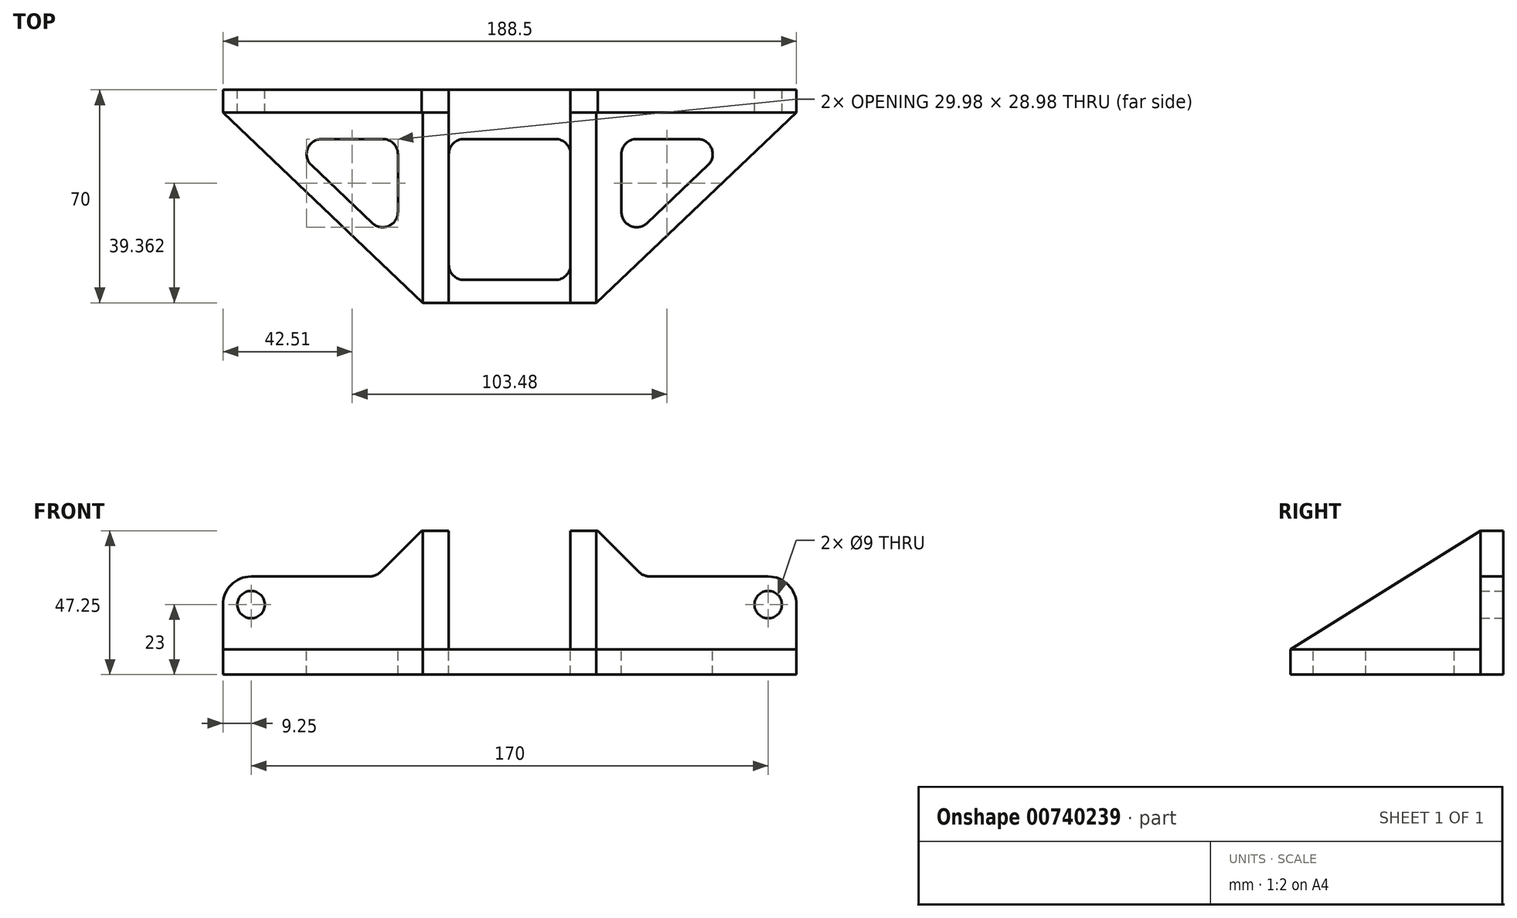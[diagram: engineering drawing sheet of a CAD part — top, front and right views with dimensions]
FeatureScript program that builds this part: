
annotation { "Feature Type Name" : "Feature", "Feature Type Description" : "" }
export const myFeature = defineFeature(function(context is Context, id is Id, definition is map)
    precondition{}
    {
        {
            var Q0;
            Q0=qCreatedBy(makeId("Front.planeOp"),FACE);
            var sketch = newSketch(context, id + "F0", { "sketchPlane" : qUnion([Q0])});
            skLineSegment(sketch, "E0", {"start": v(0, 0) * mm, "end": v(94.25, 0) * mm});
            skLineSegment(sketch, "E1", {"start": v(94.25, 0) * mm, "end": v(94.25, 23) * mm});
            skLineSegment(sketch, "E2", {"start": v(85, 32.25) * mm, "end": v(44, 32.25) * mm});
            skLineSegment(sketch, "E3", {"start": v(44, 32.25) * mm, "end": v(29, 47.25) * mm});
            skLineSegment(sketch, "E4", {"start": v(29, 47.25) * mm, "end": v(20, 47.25) * mm});
            skLineSegment(sketch, "E5", {"start": v(20, 47.25) * mm, "end": v(20, 8.25) * mm});
            skLineSegment(sketch, "E6", {"start": v(20, 8.25) * mm, "end": v(0, 8.25) * mm});
            skLineSegment(sketch, "E7", {"start": v(0, -10.9) * mm, "end": v(0, 33.84) * mm, "construction": true});
            skCircle(sketch, "E8", {"center": v(85, 23) * mm, "radius": 4.5 * mm});
            skPoint(sketch, "E9.visualSharp", {"position": v(94.25, 32.25) * mm});
            skArc(sketch, "E9.filletArc", {"start": v(94.25, 23) * mm, "mid": v(91.54, 29.54) * mm, "end": v(85, 32.25) * mm});
            skLineSegment(sketch, "E10.MirrorCS", {"start": v(-29, 47.25) * mm, "end": v(-20, 47.25) * mm});
            skPoint(sketch, "E11.MirrorP", {"position": v(-94.25, 32.25) * mm});
            skLineSegment(sketch, "E12.MirrorCS", {"start": v(0, 0) * mm, "end": v(-94.25, 0) * mm});
            skLineSegment(sketch, "E13.MirrorCS", {"start": v(-94.25, 0) * mm, "end": v(-94.25, 23) * mm});
            skLineSegment(sketch, "E14.MirrorCS", {"start": v(-44, 32.25) * mm, "end": v(-29, 47.25) * mm});
            skLineSegment(sketch, "E15.MirrorCS", {"start": v(-85, 32.25) * mm, "end": v(-44, 32.25) * mm});
            skLineSegment(sketch, "E16.MirrorCS", {"start": v(-20, 47.25) * mm, "end": v(-20, 8.25) * mm});
            skLineSegment(sketch, "E17.MirrorCS", {"start": v(-20, 8.25) * mm, "end": v(0, 8.25) * mm});
            skArc(sketch, "E18.MirrorCS", {"start": v(-94.25, 23) * mm, "mid": v(-91.54, 29.54) * mm, "end": v(-85, 32.25) * mm});
            skCircle(sketch, "E19.MirrorC", {"center": v(-85, 23) * mm, "radius": 4.5 * mm});
            skSolve(sketch);
        }
        {
            var Q0;
            Q0 = qSketchRegion(id + "F0", true);
            extrude(context, id + "F1", {"entities" : qUnion([Q0]), "depth" : 7.5 * mm, "offsetDistance" : 25.4 * mm});
        }
        {
            var Q0;
            Q0=makeQuery(id+"F1.opExtrude","CAP_FACE",FACE,{"disambiguationData":[OSD([sQuery(id+"F0.wireOp",EDGE,"E0"),sQuery(id+"F0.wireOp",EDGE,"E1"),sQuery(id+"F0.wireOp",EDGE,"E2"),sQuery(id+"F0.wireOp",EDGE,"E3"),sQuery(id+"F0.wireOp",EDGE,"E4"),sQuery(id+"F0.wireOp",EDGE,"E5"),sQuery(id+"F0.wireOp",EDGE,"E6"),sQuery(id+"F0.wireOp",EDGE,"E8"),sQuery(id+"F0.wireOp",EDGE,"E9.filletArc"),sQuery(id+"F0.wireOp",EDGE,"E10.MirrorCS"),sQuery(id+"F0.wireOp",EDGE,"E12.MirrorCS"),sQuery(id+"F0.wireOp",EDGE,"E13.MirrorCS"),sQuery(id+"F0.wireOp",EDGE,"E14.MirrorCS"),sQuery(id+"F0.wireOp",EDGE,"E15.MirrorCS"),sQuery(id+"F0.wireOp",EDGE,"E16.MirrorCS"),sQuery(id+"F0.wireOp",EDGE,"E17.MirrorCS"),sQuery(id+"F0.wireOp",EDGE,"E18.MirrorCS"),sQuery(id+"F0.wireOp",EDGE,"E19.MirrorC")])],"isStart":false});
            var sketch = newSketch(context, id + "F2", { "sketchPlane" : qUnion([Q0])});
            skLineSegment(sketch, "E20.bottom", {"start": v(-94.25, 0) * mm, "end": v(94.25, 0) * mm});
            skLineSegment(sketch, "E20.top", {"start": v(-94.25, 8.25) * mm, "end": v(94.25, 8.25) * mm});
            skLineSegment(sketch, "E20.left", {"start": v(-94.25, 0) * mm, "end": v(-94.25, 8.25) * mm});
            skLineSegment(sketch, "E20.right", {"start": v(94.25, 0) * mm, "end": v(94.25, 8.25) * mm});
            skSolve(sketch);
        }
        {
            var Q0;
            Q0 = qSketchRegion(id + "F2", true);
            extrude(context, id + "F3", {"entities" : qUnion([Q0]), "operationType" : NewBodyOperationType.ADD, "depth" : 62.5 * mm, "offsetDistance" : 25.4 * mm});
        }
        {
            var Q0;
            Q0=makeQuery(id+"F3.boolean.opBoolean","MERGE",FACE,{"derivedFrom":[makeQuery(id+"F1.opExtrude","SWEPT_FACE",FACE,{"disambiguationData":[OSD([sQuery(id+"F0.wireOp",EDGE,"E6"),sQuery(id+"F0.wireOp",EDGE,"E17.MirrorCS")])]}),makeQuery(id+"F3.opExtrude","SWEPT_FACE",FACE,{"disambiguationData":[OSD([sQuery(id+"F2.wireOp",EDGE,"E20.top")])]})]});
            var sketch = newSketch(context, id + "F4", { "sketchPlane" : qUnion([Q0])});
            skLineSegment(sketch, "E21", {"start": v(-61.75, -16.15) * mm, "end": v(-41.75, -16.15) * mm});
            skLineSegment(sketch, "E22", {"start": v(-36.75, -21.15) * mm, "end": v(-36.75, -40.16) * mm});
            skLineSegment(sketch, "E23", {"start": v(-45.2, -43.78) * mm, "end": v(-65.2, -24.77) * mm});
            skLineSegment(sketch, "E24", {"start": v(0, -16.15) * mm, "end": v(-15, -16.15) * mm});
            skLineSegment(sketch, "E25", {"start": v(-20, -21.15) * mm, "end": v(-20, -57.5) * mm});
            skLineSegment(sketch, "E26", {"start": v(-15, -62.5) * mm, "end": v(0, -62.5) * mm});
            skLineSegment(sketch, "E27", {"start": v(-94.25, -7.5) * mm, "end": v(-28.5, -70) * mm});
            skLineSegment(sketch, "E28", {"start": v(-28.5, -70) * mm, "end": v(-94.25, -70) * mm});
            skLineSegment(sketch, "E29", {"start": v(-94.25, -70) * mm, "end": v(-94.25, -7.5) * mm});
            skLineSegment(sketch, "E30", {"start": v(0, 0) * mm, "end": v(0, -70) * mm, "construction": true});
            skPoint(sketch, "E31.visualSharp", {"position": v(-36.75, -16.15) * mm});
            skArc(sketch, "E31.filletArc", {"start": v(-36.75, -21.15) * mm, "mid": v(-38.21, -17.61) * mm, "end": v(-41.75, -16.15) * mm});
            skPoint(sketch, "E32.visualSharp", {"position": v(-74.26, -16.15) * mm});
            skArc(sketch, "E32.filletArc", {"start": v(-61.75, -16.15) * mm, "mid": v(-66.4, -19.3) * mm, "end": v(-65.2, -24.77) * mm});
            skPoint(sketch, "E33.visualSharp", {"position": v(-36.75, -51.81) * mm});
            skArc(sketch, "E33.filletArc", {"start": v(-45.2, -43.78) * mm, "mid": v(-39.78, -44.75) * mm, "end": v(-36.75, -40.16) * mm});
            skPoint(sketch, "E34.visualSharp", {"position": v(-20, -62.5) * mm});
            skArc(sketch, "E34.filletArc", {"start": v(-20, -57.5) * mm, "mid": v(-18.54, -61.04) * mm, "end": v(-15, -62.5) * mm});
            skPoint(sketch, "E35.visualSharp", {"position": v(-20, -16.15) * mm});
            skArc(sketch, "E35.filletArc", {"start": v(-15, -16.15) * mm, "mid": v(-18.54, -17.61) * mm, "end": v(-20, -21.15) * mm});
            skLineSegment(sketch, "E36.MirrorCS", {"start": v(0, -16.15) * mm, "end": v(15, -16.15) * mm});
            skLineSegment(sketch, "E37.MirrorCS", {"start": v(15, -62.5) * mm, "end": v(0, -62.5) * mm});
            skArc(sketch, "E38.MirrorCS", {"start": v(20, -57.5) * mm, "mid": v(18.54, -61.04) * mm, "end": v(15, -62.5) * mm});
            skArc(sketch, "E39.MirrorCS", {"start": v(15, -16.15) * mm, "mid": v(18.54, -17.61) * mm, "end": v(20, -21.15) * mm});
            skArc(sketch, "E40.MirrorCS", {"start": v(36.75, -21.15) * mm, "mid": v(38.21, -17.61) * mm, "end": v(41.75, -16.15) * mm});
            skPoint(sketch, "E41.MirrorP", {"position": v(36.75, -51.81) * mm});
            skPoint(sketch, "E42.MirrorP", {"position": v(20, -62.5) * mm});
            skPoint(sketch, "E43.MirrorP", {"position": v(74.26, -16.15) * mm});
            skPoint(sketch, "E44.MirrorP", {"position": v(20, -16.15) * mm});
            skLineSegment(sketch, "E45.MirrorCS", {"start": v(45.2, -43.78) * mm, "end": v(65.2, -24.77) * mm});
            skLineSegment(sketch, "E46.MirrorCS", {"start": v(36.75, -21.15) * mm, "end": v(36.75, -40.16) * mm});
            skLineSegment(sketch, "E47.MirrorCS", {"start": v(61.75, -16.15) * mm, "end": v(41.75, -16.15) * mm});
            skPoint(sketch, "E48.MirrorP", {"position": v(36.75, -16.15) * mm});
            skArc(sketch, "E49.MirrorCS", {"start": v(45.2, -43.78) * mm, "mid": v(39.78, -44.75) * mm, "end": v(36.75, -40.16) * mm});
            skLineSegment(sketch, "E50.MirrorCS", {"start": v(28.5, -70) * mm, "end": v(94.25, -70) * mm});
            skLineSegment(sketch, "E51.MirrorCS", {"start": v(20, -21.15) * mm, "end": v(20, -57.5) * mm});
            skLineSegment(sketch, "E52.MirrorCS", {"start": v(94.25, -7.5) * mm, "end": v(28.5, -70) * mm});
            skLineSegment(sketch, "E53.MirrorCS", {"start": v(94.25, -70) * mm, "end": v(94.25, -7.5) * mm});
            skArc(sketch, "E54.MirrorCS", {"start": v(61.75, -16.15) * mm, "mid": v(66.4, -19.3) * mm, "end": v(65.2, -24.77) * mm});
            skSolve(sketch);
        }
        {
            var Q0;
            Q0 = qSketchRegion(id + "F4", true);
            var Q1;
            Q1=makeQuery(id+"F3.boolean.opBoolean","MERGE",FACE,{"derivedFrom":[makeQuery(id+"F1.opExtrude","SWEPT_FACE",FACE,{"disambiguationData":[OSD([sQuery(id+"F0.wireOp",EDGE,"E0"),sQuery(id+"F0.wireOp",EDGE,"E12.MirrorCS")])]}),makeQuery(id+"F3.opExtrude","SWEPT_FACE",FACE,{"disambiguationData":[OSD([sQuery(id+"F2.wireOp",EDGE,"E20.bottom")])]})]});
            extrude(context, id + "F5", {"entities" : qUnion([Q0]), "operationType" : NewBodyOperationType.REMOVE, "endBound" : BoundingType.UP_TO_SURFACE, "oppositeDirection" : true, "depth" : 25.4 * mm, "endBoundEntityFace" : qUnion([Q1]), "offsetDistance" : 25.4 * mm});
        }
        {
            var Q0;
            Q0=makeQuery(id+"F1.opExtrude","SWEPT_FACE",FACE,{"disambiguationData":[OSD([sQuery(id+"F0.wireOp",EDGE,"E16.MirrorCS")])]});
            var sketch = newSketch(context, id + "F6", { "sketchPlane" : qUnion([Q0])});
            skLineSegment(sketch, "E55", {"start": v(-7.5, 47.25) * mm, "end": v(-7.5, 8.25) * mm});
            skLineSegment(sketch, "E56", {"start": v(-7.5, 8.25) * mm, "end": v(-70, 8.25) * mm});
            skLineSegment(sketch, "E57", {"start": v(-70, 8.25) * mm, "end": v(-7.5, 47.25) * mm});
            skSolve(sketch);
        }
        {
            var Q0;
            Q0 = qSketchRegion(id + "F6", true);
            extrude(context, id + "F7", {"entities" : qUnion([Q0]), "operationType" : NewBodyOperationType.ADD, "oppositeDirection" : true, "depth" : 8.5 * mm, "offsetDistance" : 25.4 * mm});
        }
        {
            var Q0;
            Q0=makeQuery(id+"F1.opExtrude","SWEPT_FACE",FACE,{"disambiguationData":[OSD([sQuery(id+"F0.wireOp",EDGE,"E5")])]});
            var sketch = newSketch(context, id + "F8", { "sketchPlane" : qUnion([Q0])});
            skLineSegment(sketch, "E58", {"start": v(7.5, 47.25) * mm, "end": v(7.5, 8.25) * mm});
            skLineSegment(sketch, "E59", {"start": v(7.5, 8.25) * mm, "end": v(70, 8.25) * mm});
            skLineSegment(sketch, "E60", {"start": v(70, 8.25) * mm, "end": v(7.5, 47.25) * mm});
            skSolve(sketch);
        }
        {
            var Q0;
            Q0 = qSketchRegion(id + "F8", true);
            extrude(context, id + "F9", {"entities" : qUnion([Q0]), "operationType" : NewBodyOperationType.ADD, "oppositeDirection" : true, "depth" : 8.5 * mm, "offsetDistance" : 25.4 * mm});
        }
        {
            var Q0;
            Q0=makeQuery(id+"F5.boolean.opBoolean","COPY",EDGE,{"derivedFrom":makeQuery(id+"F5.opExtrude","SWEPT_EDGE",EDGE,{"disambiguationData":[OSD([sQuery(id+"F2.wireOp",EDGE,"E20.top"),sQuery(id+"F4.wireOp",EDGE,"E27"),sQuery(id+"F4.wireOp",EDGE,"E28")])]})});
            var Q1;
            Q1=makeQuery(id+"F5.boolean.opBoolean","COPY",EDGE,{"derivedFrom":makeQuery(id+"F5.opExtrude","SWEPT_EDGE",EDGE,{"disambiguationData":[OSD([sQuery(id+"F2.wireOp",EDGE,"E20.top"),sQuery(id+"F4.wireOp",EDGE,"E50.MirrorCS"),sQuery(id+"F4.wireOp",EDGE,"E52.MirrorCS")])]})});
            var Q2;
            Q2=makeQuery(id+"F5.boolean.opBoolean","COPY",EDGE,{"derivedFrom":makeQuery(id+"F5.opExtrude","SWEPT_EDGE",EDGE,{"disambiguationData":[OSD([sQuery(id+"F2.wireOp",EDGE,"E20.top"),sQuery(id+"F4.wireOp",EDGE,"E52.MirrorCS"),sQuery(id+"F4.wireOp",EDGE,"E53.MirrorCS")])]})});
            var Q3;
            Q3=makeQuery(id+"F5.boolean.opBoolean","COPY",EDGE,{"derivedFrom":makeQuery(id+"F5.opExtrude","SWEPT_EDGE",EDGE,{"disambiguationData":[OSD([sQuery(id+"F2.wireOp",EDGE,"E20.top"),sQuery(id+"F4.wireOp",EDGE,"E27"),sQuery(id+"F4.wireOp",EDGE,"E29")])]})});
            var Q4;
            Q4=makeQuery(id+"F1.opExtrude","SWEPT_EDGE",EDGE,{"disambiguationData":[OSD([sQuery(id+"F0.wireOp",EDGE,"E14.MirrorCS"),sQuery(id+"F0.wireOp",EDGE,"E15.MirrorCS")])]});
            var Q5;
            Q5=makeQuery(id+"F1.opExtrude","SWEPT_EDGE",EDGE,{"disambiguationData":[OSD([sQuery(id+"F0.wireOp",EDGE,"E2"),sQuery(id+"F0.wireOp",EDGE,"E3")])]});
            fillet(context, id + "F10", {"entities" : qUnion([Q0, Q1, Q2, Q3, Q4, Q5]), "radius" : 5 * mm, "tangentPropagation" : true, "allowEdgeOverflow" : false});
        }
    });
